# Revit family: Smoothy 2.4
name_source: partatom
category: Lighting Fixtures
revit_build: Autodesk Revit 2017 (Build: 20160225_1515(x64)
units: mm (PartAtom-declared; Revit-internal decimal feet)

## family parameters
Cut with Voids When Loaded = Yes
Host = Face
Light Source = Yes
Part Type = Normal
Room Calculation Point = Yes
Round Connector Dimension = Use Diameter
Shared = No

## types (10) — shared parameters
Apparent Load = 0 VA
Apparent Load Phase 1 = 7 W
Body = L&L_Anodized aluminium
CRI = 90 (also available: CRI 80 - ref. URL Technical sheet)
Code = SY240 I; SY2432 6 I
Color Filter = 16777215
Control system = -
Cutout dimensions = diam. 75 mm
Default Elevation = 1219 mm
Delivered lumen output = 352 lm (3000K, 34°, 5W, CRI 80); 284 lm (3000K, 34°, 5W, CRI 90); 463 lm (3000K, 34°, 7W, CRI 80); 374 lm (3000K, 34°, 7W, CRI 90); RGB: 235 lm, R: 92 lm G: 105 lm B: 38 lm (700mA, 34°)
Description = recessed for outdoor applications
Dimming Lamp Color Temperature Shift = <None>
Emit from Line Length = 610 mm
Energy efficiency class = A A+ A++
Features = -
Geometry = Smoothy2.4_mod
Height Void = 67 mm
Height mm = 67 mm
IP = 67
LED Colour = 3000K (also available: 2700K and 4000K - ref. URL Technical sheet)
Length mm = 84 mm  [stored 0.275591 ft]
Lens = L&L_Tempered extra-clear glass
Lumen output at source = 488 lm (3000K, 5W, CRI 80); 452 lm (3000K, 5W, CRI 90); 657 lm (3000K, 7W, CRI 80); 608 lm (3000K, 7W, CRI 90); RGB: 311 lm, R: 108 lm G: 133 lm B: 70 lm (700mA)
Manufacturer = L&L Luce&Light
Material = body in anodized aluminium, trim in AISI 316L stainless steelscreen in tempered, transparent extra-clear glass (optics version), screen in sandblasted, tempered extra-clear glass (diffuse version)
Model = Smoothy 2.4
Mounting = recessed (ceiling, wall, ground)
No. and type of led = 1 high-intensity power LED; RGB: 3 power LEDs
Notes = -
Power = 7W (also available: 3,5W only 5°optics (4000K only CRI 80) and 5W - ref. URL Technical sheet)
Power cables = includes 1.5 m neoprene cable; H05RN-F 2x0.75/0.75 Ø6.3 mm; RGB: includes 1.5 m FEP+RUB (equivalent to H05RN-F) 6x0.50/0.50 Ø6.3 mm
Power supply = 24Vdc (also available: max 700mA RGB light - ref. URL Technical sheet)
Power supply unit = not included
Radius Void = 38 mm
Tilt Angle = 90.00°
Tiltable = -
Trim = L&L_Steel inox AISI 316L
URL = https://www.lucelight.it
URL Accessories and power supply units = https://www.lucelight.it
URL Catalogue = https://www.lucelight.it
URL DXF = https://www.lucelight.it
URL Description = https://www.lucelight.it
URL General code = https://www.lucelight.it
URL IES Photometric file = https://www.lucelight.it
URL Image = https://www.lucelight.it
URL Technical sheet = https://www.lucelight.it
Voltage = 24 V
Weight kg = 0.43
Width mm = 84 mm  [stored 0.275591 ft]
Wiring = parallel; RGB: series

## per-type parameters (varying)
| type | Optics | Photometric Web File |
| Smoothy 2.4_D (3000K 7W 24Vdc) | D | SMOOTHY 2.4 D [3000K 7W 24Vdc].IES |
| Smoothy 2.4_L 45° (3000K 7W 24Vdc) | 45° | SMOOTHY 2.4 L 45° [3000K 7W 24Vdc].IES |
| Smoothy 2.4_M 34° (3000K 7W 24Vdc) | 34° | SMOOTHY 2.4 M 34° [3000K 7W 24Vdc].IES |
| Smoothy 2.4_P 21° (3000K 7W 24Vdc) | 21° | SMOOTHY 2.4 P (21°) [3000K 7W 24Vdc].IES |
| Smoothy 2.4_Q 61° (3000K 7W 24Vdc) | 61° | SMOOTHY 2.4 Q (61°) [3000K 7W 24Vdc].IES |
| Smoothy 2.4_S 17° (3000K 7W 24Vdc) | 17° | SMOOTHY 2.4 S 17° [3000K 7W 24Vdc].IES |
| Smoothy 2.4_T 11° (3000K 7W 24Vdc) | 11° | SMOOTHY 2.4 T 11° [3000K 7W 24Vdc].IES |
| Smoothy 2.4_U 5° (3000K 3.5W 24Vdc) | 5° | SMOOTHY 2.4 U 5° [3000K 3.5W 24Vdc].IES |
| Smoothy 2.4_V 8° (3000K 7W 24Vdc) | 8° | SMOOTHY 2.4 V 8° [3000K 7W 24Vdc].IES |
| Smoothy 2.4_W 13°x52° (3000K 7W 24Vdc) | 13°x52° | SMOOTHY 2.4 W 13°x52° [3000K 7W 24Vdc].IES |

note: [stored X ft] marks values corroborated as IEEE doubles in the binary element streams (Revit-internal decimal feet)

## geometry (parser evidence)
native form markers: Blend x2, Sweep x10
no freeform markers — native parametric forms only
